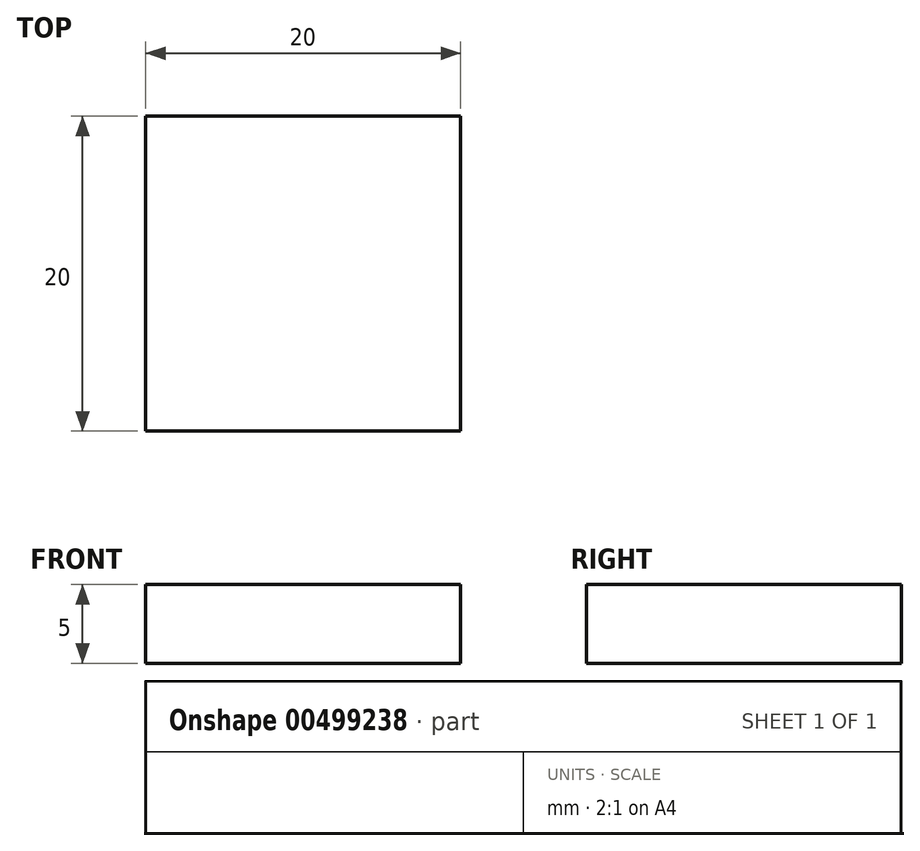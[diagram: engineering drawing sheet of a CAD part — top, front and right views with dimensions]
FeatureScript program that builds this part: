
annotation { "Feature Type Name" : "Feature", "Feature Type Description" : "" }
export const myFeature = defineFeature(function(context is Context, id is Id, definition is map)
    precondition{}
    {
        {
            var Q0;
            Q0=qCreatedBy(makeId("Top.planeOp"),FACE);
            var sketch = newSketch(context, id + "F0", { "sketchPlane" : qUnion([Q0])});
            skLineSegment(sketch, "E0.bottom", {"start": v(12.48, -10) * mm, "end": v(-7.52, -10) * mm});
            skLineSegment(sketch, "E0.top", {"start": v(12.48, 10) * mm, "end": v(-7.52, 10) * mm});
            skLineSegment(sketch, "E0.left", {"start": v(12.48, -10) * mm, "end": v(12.48, 10) * mm});
            skLineSegment(sketch, "E0.right", {"start": v(-7.52, -10) * mm, "end": v(-7.52, 10) * mm});
            skPoint(sketch, "E0.middle", {"position": v(2.48, 0) * mm});
            skSolve(sketch);
        }
        {
            var Q0;
            Q0=makeQuery(id+"F0.imprint","IMPRINT",FACE,{"disambiguationData":[TD([[makeQuery(id+"F0.imprint","IMPRINT",EDGE,{"derivedFrom":sQuery(id+"F0.wireOp",EDGE,"E0.bottom")}),-1.0]])]});
            extrude(context, id + "F1", {"entities" : qUnion([Q0]), "depth" : 5 * mm});
        }
    });
